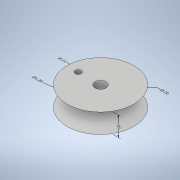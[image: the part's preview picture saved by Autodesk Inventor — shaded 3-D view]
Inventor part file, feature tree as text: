
AUTODESK INVENTOR PART (.ipt)
format: ipt  version: 2020 (Build 240168000, 168)  size: 144,384 bytes
history: native  units: in
note: dims shown in document units (in); Inventor stores cm internally (conversion verified against a paired STEP export)
features: sketch x4, extrude x2, draft x2, hole x2
ambient origin geometry x8: Origin, YZ Plane, XZ Plane, XY Plane, X Axis, Y Axis, Z Axis, Center Point
bodies: Solid1 (feature_tree)
feature tree (10):
  extrude  "Extrusion1"  Depth=0.175in TaperAngle=0.0deg
  draft  "FaceDraft1"
  extrude  "Extrusion2"  Depth=0.175in TaperAngle=0.0deg
  draft  "FaceDraft2"
  hole  "Hole1"  [1 undecoded]
  hole  "Hole2"  [1 undecoded]
  sketch  "Sketch1"  dims[d0=1.2in d1=0.175in d2=0.0in]
  sketch  "Sketch2"  dims[d3=60.0deg d4=0.175in d5=0.0in]
  sketch  "Sketch3"  dims[d6=60.0deg]
  sketch  "Sketch4"  dims[d7=0.2in d8=0.75in d9=0.375in d10=0.25in d11=0.5635in d12=1.0in d13=0.8108in d14=0.3in d15=0.11in d16=0.75in d17=0.375in d18=0.25in d19=0.5635in d20=1.0in d21=0.8108in d22=1.4318in d23=0.1967in d24=0.2828in d25=0.11in d26=2.1708in d27=0.0466in d28=0.2461in d29=0.2in d30=1.1782in d31=1.2in d32=0.2988in d33=0.2534in d34=0.35in]
note: 2 required parameter values undecoded (feature->parameter linkage not recoverable at this tier; creation-order binding heuristic only, values carry confidence <= 0.55)
